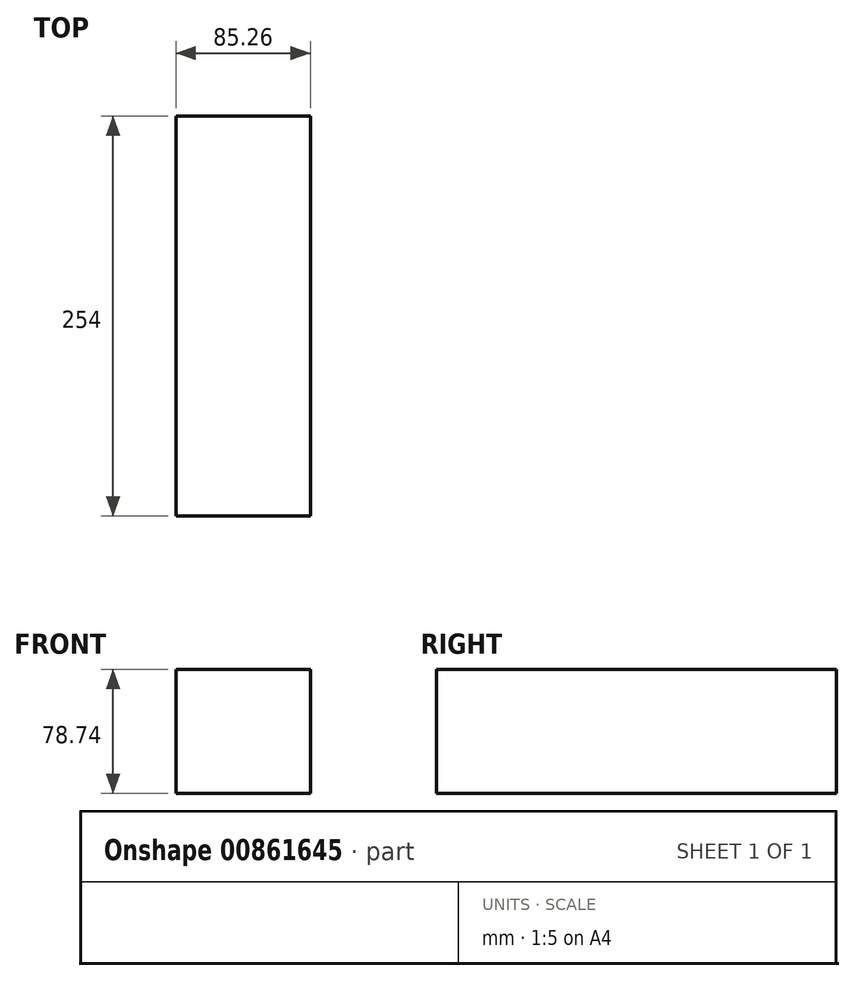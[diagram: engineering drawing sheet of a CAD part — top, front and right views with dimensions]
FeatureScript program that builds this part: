
annotation { "Feature Type Name" : "Feature", "Feature Type Description" : "" }
export const myFeature = defineFeature(function(context is Context, id is Id, definition is map)
    precondition{}
    {
        {
            var Q0;
            Q0=qCreatedBy(makeId("Front.planeOp"),FACE);
            var sketch = newSketch(context, id + "F0", { "sketchPlane" : qUnion([Q0])});
            skLineSegment(sketch, "E0.bottom", {"start": v(42.63, -39.37) * mm, "end": v(-42.63, -39.37) * mm});
            skLineSegment(sketch, "E0.top", {"start": v(42.63, 39.37) * mm, "end": v(-42.63, 39.37) * mm});
            skLineSegment(sketch, "E0.left", {"start": v(42.63, -39.37) * mm, "end": v(42.63, 39.37) * mm});
            skLineSegment(sketch, "E0.right", {"start": v(-42.63, -39.37) * mm, "end": v(-42.63, 39.37) * mm});
            skPoint(sketch, "E0.middle", {"position": v(0, 0) * mm});
            skSolve(sketch);
        }
        {
            var Q0;
            Q0=makeQuery(id+"F0.imprint","IMPRINT",FACE,{"disambiguationData":[TD([[makeQuery(id+"F0.imprint","IMPRINT",EDGE,{"derivedFrom":sQuery(id+"F0.wireOp",EDGE,"E0.bottom")}),-1.0]])]});
            extrude(context, id + "F1", {"entities" : qUnion([Q0]), "endBound" : BoundingType.SYMMETRIC, "depth" : 254 * mm, "offsetDistance" : 25.4 * mm});
        }
    });
